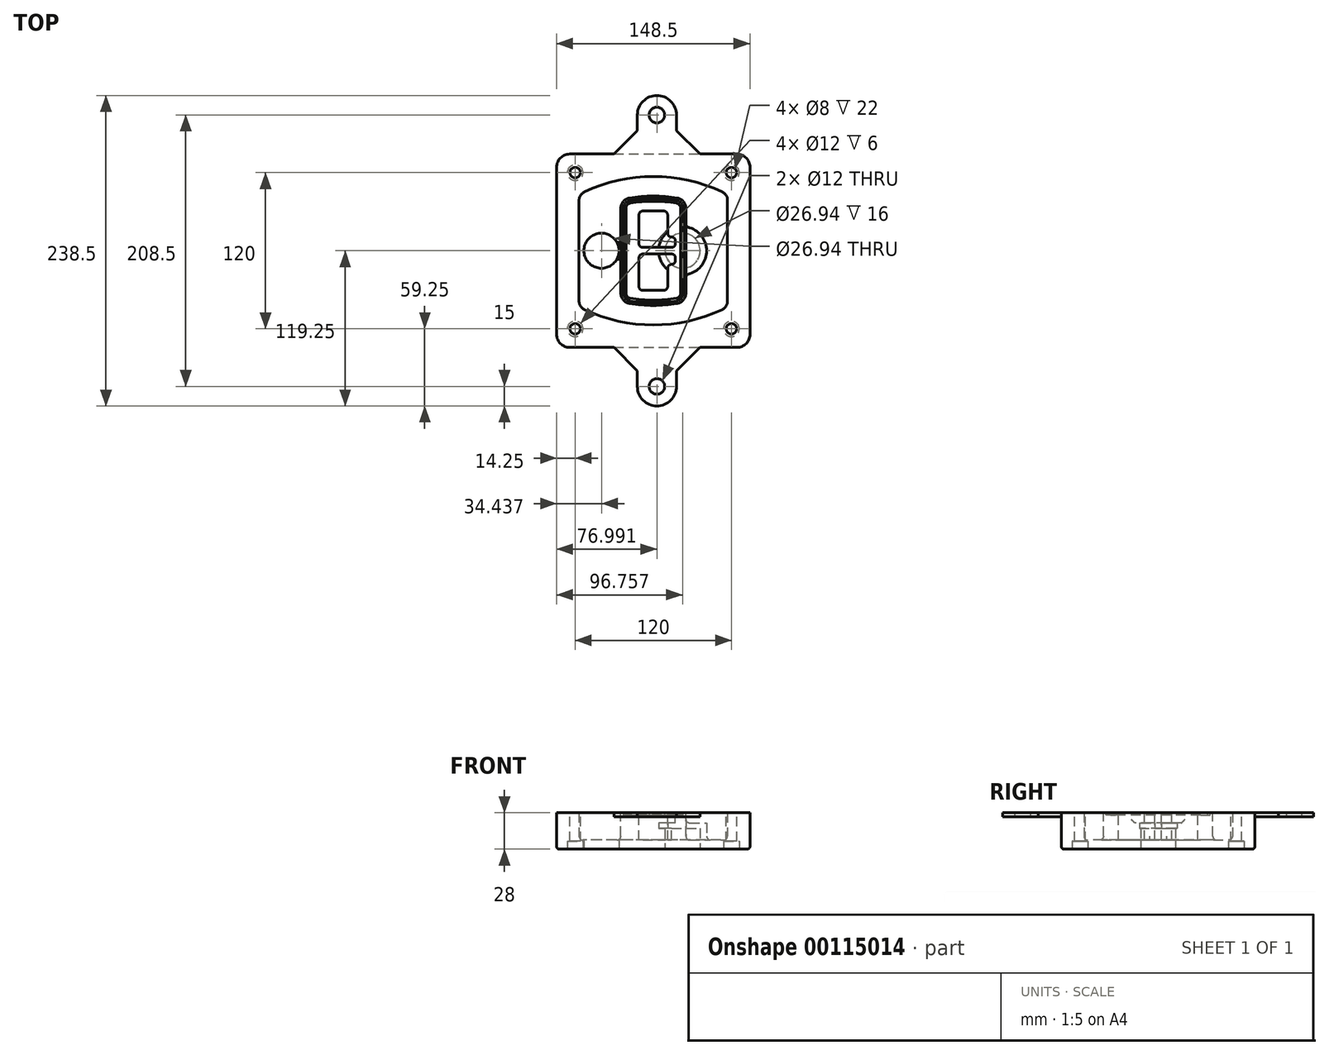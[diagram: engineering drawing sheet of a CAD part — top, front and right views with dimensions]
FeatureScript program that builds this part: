
annotation { "Feature Type Name" : "Feature", "Feature Type Description" : "" }
export const myFeature = defineFeature(function(context is Context, id is Id, definition is map)
    precondition{}
    {
        {
            var Q0;
            Q0=qCreatedBy(makeId("Top.planeOp"),FACE);
            var sketch = newSketch(context, id + "F0", { "sketchPlane" : qUnion([Q0])});
            skPoint(sketch, "E0.rect.middle", {"position": v(0, 0) * mm});
            skLineSegment(sketch, "E1.bottom", {"start": v(-64.25, -74.25) * mm, "end": v(64.25, -74.25) * mm});
            skLineSegment(sketch, "E1.top", {"start": v(-64.25, 74.25) * mm, "end": v(64.25, 74.25) * mm});
            skLineSegment(sketch, "E1.left", {"start": v(-74.25, -64.25) * mm, "end": v(-74.25, 64.25) * mm});
            skLineSegment(sketch, "E1.right", {"start": v(74.25, -64.25) * mm, "end": v(74.25, 64.25) * mm});
            skLineSegment(sketch, "E2", {"start": v(-74.25, 74.25) * mm, "end": v(74.25, -74.25) * mm, "construction": true});
            skLineSegment(sketch, "E3", {"start": v(74.25, 74.25) * mm, "end": v(-74.25, -74.25) * mm, "construction": true});
            skCircle(sketch, "E4", {"center": v(-60, 60) * mm, "radius": 4 * mm});
            skCircle(sketch, "E5", {"center": v(60, 60) * mm, "radius": 4 * mm});
            skCircle(sketch, "E6", {"center": v(60, -60) * mm, "radius": 4 * mm});
            skCircle(sketch, "E7", {"center": v(-60, -60) * mm, "radius": 4 * mm});
            skLineSegment(sketch, "E8", {"start": v(-60, 60) * mm, "end": v(60, 60) * mm, "construction": true});
            skLineSegment(sketch, "E9", {"start": v(60, 60) * mm, "end": v(60, -60) * mm, "construction": true});
            skLineSegment(sketch, "E10", {"start": v(60, -60) * mm, "end": v(-60, -60) * mm, "construction": true});
            skLineSegment(sketch, "E11", {"start": v(-60, -60) * mm, "end": v(-60, 60) * mm, "construction": true});
            skLineSegment(sketch, "E12", {"start": v(-60, 38.83) * mm, "end": v(-60, -38.83) * mm});
            skLineSegment(sketch, "E13", {"start": v(60, 38.83) * mm, "end": v(60, -38.83) * mm});
            skArc(sketch, "E14", {"start": v(54.26, 47.88) * mm, "mid": v(0, 60) * mm, "end": v(-54.26, 47.88) * mm});
            skArc(sketch, "E15", {"start": v(-54.26, -47.88) * mm, "mid": v(0, -60) * mm, "end": v(54.26, -47.88) * mm});
            skLineSegment(sketch, "E16", {"start": v(-60, 0) * mm, "end": v(60, 0) * mm, "construction": true});
            skPoint(sketch, "E17.visualSharp", {"position": v(-60, -45) * mm});
            skArc(sketch, "E17.filletArc", {"start": v(-60, -38.83) * mm, "mid": v(-58.44, -44.2) * mm, "end": v(-54.26, -47.88) * mm});
            skPoint(sketch, "E18.visualSharp", {"position": v(-60, 45) * mm});
            skArc(sketch, "E18.filletArc", {"start": v(-54.26, 47.88) * mm, "mid": v(-58.44, 44.2) * mm, "end": v(-60, 38.83) * mm});
            skPoint(sketch, "E19.visualSharp", {"position": v(60, 45) * mm});
            skArc(sketch, "E19.filletArc", {"start": v(60, 38.83) * mm, "mid": v(58.44, 44.2) * mm, "end": v(54.26, 47.88) * mm});
            skPoint(sketch, "E20.visualSharp", {"position": v(60, -45) * mm});
            skArc(sketch, "E20.filletArc", {"start": v(54.26, -47.88) * mm, "mid": v(58.44, -44.2) * mm, "end": v(60, -38.83) * mm});
            skPoint(sketch, "E21.visualSharp", {"position": v(-74.25, 74.25) * mm});
            skArc(sketch, "E21.filletArc", {"start": v(-64.25, 74.25) * mm, "mid": v(-71.32, 71.32) * mm, "end": v(-74.25, 64.25) * mm});
            skPoint(sketch, "E22.visualSharp", {"position": v(74.25, 74.25) * mm});
            skArc(sketch, "E22.filletArc", {"start": v(74.25, 64.25) * mm, "mid": v(71.32, 71.32) * mm, "end": v(64.25, 74.25) * mm});
            skPoint(sketch, "E23.visualSharp", {"position": v(74.25, -74.25) * mm});
            skArc(sketch, "E23.filletArc", {"start": v(64.25, -74.25) * mm, "mid": v(71.32, -71.32) * mm, "end": v(74.25, -64.25) * mm});
            skPoint(sketch, "E24.visualSharp", {"position": v(-74.25, -74.25) * mm});
            skArc(sketch, "E24.filletArc", {"start": v(-74.25, -64.25) * mm, "mid": v(-71.32, -71.32) * mm, "end": v(-64.25, -74.25) * mm});
            skArc(sketch, "E25.0", {"start": v(57, 38.83) * mm, "mid": v(55.9, 42.58) * mm, "end": v(52.98, 45.17) * mm});
            skLineSegment(sketch, "E25.1", {"start": v(57, 38.83) * mm, "end": v(57, -38.83) * mm});
            skArc(sketch, "E25.2", {"start": v(52.98, -45.17) * mm, "mid": v(55.9, -42.58) * mm, "end": v(57, -38.83) * mm});
            skArc(sketch, "E25.3", {"start": v(-52.98, -45.17) * mm, "mid": v(0, -57) * mm, "end": v(52.98, -45.17) * mm});
            skArc(sketch, "E25.4", {"start": v(-57, -38.83) * mm, "mid": v(-55.9, -42.58) * mm, "end": v(-52.98, -45.17) * mm});
            skArc(sketch, "E25.5", {"start": v(52.98, 45.17) * mm, "mid": v(0, 57) * mm, "end": v(-52.98, 45.17) * mm});
            skLineSegment(sketch, "E25.6", {"start": v(-57, 38.83) * mm, "end": v(-57, -38.83) * mm});
            skArc(sketch, "E25.7", {"start": v(-52.98, 45.17) * mm, "mid": v(-55.9, 42.58) * mm, "end": v(-57, 38.83) * mm});
            skArc(sketch, "E26.0", {"start": v(-55.96, 51.5) * mm, "mid": v(-61.82, 46.33) * mm, "end": v(-64, 38.83) * mm});
            skArc(sketch, "E26.1", {"start": v(55.96, 51.5) * mm, "mid": v(0, 64) * mm, "end": v(-55.96, 51.5) * mm});
            skArc(sketch, "E26.2", {"start": v(64, 38.83) * mm, "mid": v(61.82, 46.33) * mm, "end": v(55.96, 51.5) * mm});
            skLineSegment(sketch, "E26.3", {"start": v(64, 38.83) * mm, "end": v(64, -38.83) * mm});
            skArc(sketch, "E26.4", {"start": v(55.96, -51.5) * mm, "mid": v(61.82, -46.33) * mm, "end": v(64, -38.83) * mm});
            skLineSegment(sketch, "E26.5", {"start": v(-64, 38.83) * mm, "end": v(-64, -38.83) * mm});
            skArc(sketch, "E26.6", {"start": v(-55.96, -51.5) * mm, "mid": v(0, -64) * mm, "end": v(55.96, -51.5) * mm});
            skArc(sketch, "E26.7", {"start": v(-64, -38.83) * mm, "mid": v(-61.82, -46.33) * mm, "end": v(-55.96, -51.5) * mm});
            skSolve(sketch);
        }
        {
            var Q0;
            Q0=makeQuery(id+"F0.imprint","IMPRINT",FACE,{"disambiguationData":[TD([[makeQuery(id+"F0.imprint","IMPRINT",EDGE,{"derivedFrom":sQuery(id+"F0.wireOp",EDGE,"E1.bottom")}),1.0]])]});
            var Q1;
            Q1=makeQuery(id+"F0.imprint","IMPRINT",FACE,{"disambiguationData":[TD([[makeQuery(id+"F0.imprint","IMPRINT",EDGE,{"derivedFrom":sQuery(id+"F0.wireOp",EDGE,"E12")}),1.0]])]});
            var Q2;
            Q2=makeQuery(id+"F0.imprint","IMPRINT",FACE,{"disambiguationData":[TD([[makeQuery(id+"F0.imprint","IMPRINT",EDGE,{"derivedFrom":sQuery(id+"F0.wireOp",EDGE,"E25.0")}),1.0]])]});
            var Q3;
            Q3=makeQuery(id+"F0.imprint","IMPRINT",FACE,{"disambiguationData":[TD([[makeQuery(id+"F0.imprint","IMPRINT",EDGE,{"derivedFrom":sQuery(id+"F0.wireOp",EDGE,"E12")}),-1.0]])]});
            extrude(context, id + "F1", {"entities" : qUnion([Q0, Q1, Q2, Q3]), "oppositeDirection" : true, "depth" : 25 * mm});
        }
        {
            var Q0;
            Q0=makeQuery(id+"F0.imprint","IMPRINT",FACE,{"disambiguationData":[TD([[makeQuery(id+"F0.imprint","IMPRINT",EDGE,{"derivedFrom":sQuery(id+"F0.wireOp",EDGE,"E12")}),1.0]])]});
            extrude(context, id + "F2", {"entities" : qUnion([Q0]), "operationType" : NewBodyOperationType.ADD, "depth" : 3 * mm});
        }
        {
            var Q0;
            Q0=makeQuery(id+"F0.imprint","IMPRINT",FACE,{"disambiguationData":[TD([[makeQuery(id+"F0.imprint","IMPRINT",EDGE,{"derivedFrom":sQuery(id+"F0.wireOp",EDGE,"E25.0")}),1.0]])]});
            extrude(context, id + "F3", {"entities" : qUnion([Q0]), "operationType" : NewBodyOperationType.REMOVE, "oppositeDirection" : true, "depth" : 18 * mm});
        }
        {
            var Q0;
            Q0=makeQuery(id+"F2.opExtrude","CAP_FACE",FACE,{"disambiguationData":[OSD([sQuery(id+"F0.wireOp",EDGE,"E12"),sQuery(id+"F0.wireOp",EDGE,"E13"),sQuery(id+"F0.wireOp",EDGE,"E14"),sQuery(id+"F0.wireOp",EDGE,"E15"),sQuery(id+"F0.wireOp",EDGE,"E17.filletArc"),sQuery(id+"F0.wireOp",EDGE,"E18.filletArc"),sQuery(id+"F0.wireOp",EDGE,"E19.filletArc"),sQuery(id+"F0.wireOp",EDGE,"E20.filletArc"),sQuery(id+"F0.wireOp",EDGE,"E25.0"),sQuery(id+"F0.wireOp",EDGE,"E25.1"),sQuery(id+"F0.wireOp",EDGE,"E25.2"),sQuery(id+"F0.wireOp",EDGE,"E25.3"),sQuery(id+"F0.wireOp",EDGE,"E25.4"),sQuery(id+"F0.wireOp",EDGE,"E25.5"),sQuery(id+"F0.wireOp",EDGE,"E25.6"),sQuery(id+"F0.wireOp",EDGE,"E25.7")])],"isStart":false});
            var sketch = newSketch(context, id + "F4", { "sketchPlane" : qUnion([Q0])});
            skArc(sketch, "E27.0", {"start": v(-18.34, -40.45) * mm, "mid": v(0, -42) * mm, "end": v(18.34, -40.45) * mm});
            skArc(sketch, "E28.0", {"start": v(18.34, 40.45) * mm, "mid": v(0, 42) * mm, "end": v(-18.34, 40.45) * mm});
            skLineSegment(sketch, "E29", {"start": v(-25, 32.57) * mm, "end": v(-25, -32.57) * mm});
            skLineSegment(sketch, "E30", {"start": v(25, 32.57) * mm, "end": v(25, -32.57) * mm});
            skLineSegment(sketch, "E31", {"start": v(-25, 39.1) * mm, "end": v(25, 39.1) * mm, "construction": true});
            skLineSegment(sketch, "E32", {"start": v(-25, -39.1) * mm, "end": v(25, -39.1) * mm, "construction": true});
            skPoint(sketch, "E33.visualSharp", {"position": v(-25, 39.1) * mm});
            skArc(sketch, "E33.filletArc", {"start": v(-18.34, 40.45) * mm, "mid": v(-23.11, 37.73) * mm, "end": v(-25, 32.57) * mm});
            skPoint(sketch, "E34.visualSharp", {"position": v(25, 39.1) * mm});
            skArc(sketch, "E34.filletArc", {"start": v(25, 32.57) * mm, "mid": v(23.11, 37.73) * mm, "end": v(18.34, 40.45) * mm});
            skPoint(sketch, "E35.visualSharp", {"position": v(25, -39.1) * mm});
            skArc(sketch, "E35.filletArc", {"start": v(18.34, -40.45) * mm, "mid": v(23.11, -37.73) * mm, "end": v(25, -32.57) * mm});
            skPoint(sketch, "E36.visualSharp", {"position": v(-25, -39.1) * mm});
            skArc(sketch, "E36.filletArc", {"start": v(-25, -32.57) * mm, "mid": v(-23.11, -37.73) * mm, "end": v(-18.34, -40.45) * mm});
            skArc(sketch, "E37.0", {"start": v(52.98, 45.17) * mm, "mid": v(0, 57) * mm, "end": v(-52.98, 45.17) * mm});
            skArc(sketch, "E37.1", {"start": v(-52.98, 45.17) * mm, "mid": v(-55.9, 42.58) * mm, "end": v(-57, 38.83) * mm});
            skLineSegment(sketch, "E37.2", {"start": v(-57, 38.83) * mm, "end": v(-57, -38.83) * mm});
            skArc(sketch, "E37.3", {"start": v(-57, -38.83) * mm, "mid": v(-55.9, -42.58) * mm, "end": v(-52.98, -45.17) * mm});
            skArc(sketch, "E37.4", {"start": v(-52.98, -45.17) * mm, "mid": v(0, -57) * mm, "end": v(52.98, -45.17) * mm});
            skArc(sketch, "E37.5", {"start": v(52.98, -45.17) * mm, "mid": v(55.9, -42.58) * mm, "end": v(57, -38.83) * mm});
            skLineSegment(sketch, "E37.6", {"start": v(57, 38.83) * mm, "end": v(57, -38.83) * mm});
            skArc(sketch, "E37.7", {"start": v(57, 38.83) * mm, "mid": v(55.9, 42.58) * mm, "end": v(52.98, 45.17) * mm});
            skLineSegment(sketch, "E38.0", {"start": v(23, 32.57) * mm, "end": v(23, -32.57) * mm});
            skArc(sketch, "E38.1", {"start": v(18, -38.48) * mm, "mid": v(21.58, -36.44) * mm, "end": v(23, -32.57) * mm});
            skArc(sketch, "E38.2", {"start": v(-18, -38.48) * mm, "mid": v(0, -40) * mm, "end": v(18, -38.48) * mm});
            skArc(sketch, "E38.3", {"start": v(-23, -32.57) * mm, "mid": v(-21.58, -36.44) * mm, "end": v(-18, -38.48) * mm});
            skLineSegment(sketch, "E38.4", {"start": v(-23, 32.57) * mm, "end": v(-23, -32.57) * mm});
            skArc(sketch, "E38.5", {"start": v(23, 32.57) * mm, "mid": v(21.58, 36.44) * mm, "end": v(18, 38.48) * mm});
            skArc(sketch, "E38.6", {"start": v(-18, 38.48) * mm, "mid": v(-21.58, 36.44) * mm, "end": v(-23, 32.57) * mm});
            skArc(sketch, "E38.7", {"start": v(18, 38.48) * mm, "mid": v(0, 40) * mm, "end": v(-18, 38.48) * mm});
            skArc(sketch, "E39.0", {"start": v(21, 32.57) * mm, "mid": v(20.06, 35.15) * mm, "end": v(17.67, 36.5) * mm});
            skLineSegment(sketch, "E39.1", {"start": v(21, 32.57) * mm, "end": v(21, -32.57) * mm});
            skArc(sketch, "E39.2", {"start": v(17.67, -36.5) * mm, "mid": v(20.06, -35.15) * mm, "end": v(21, -32.57) * mm});
            skArc(sketch, "E39.3", {"start": v(-17.67, -36.5) * mm, "mid": v(0, -38) * mm, "end": v(17.67, -36.5) * mm});
            skArc(sketch, "E39.4", {"start": v(-21, -32.57) * mm, "mid": v(-20.06, -35.15) * mm, "end": v(-17.67, -36.5) * mm});
            skArc(sketch, "E39.5", {"start": v(17.67, 36.5) * mm, "mid": v(0, 38) * mm, "end": v(-17.67, 36.5) * mm});
            skLineSegment(sketch, "E39.6", {"start": v(-21, 32.57) * mm, "end": v(-21, -32.57) * mm});
            skArc(sketch, "E39.7", {"start": v(-17.67, 36.5) * mm, "mid": v(-20.06, 35.15) * mm, "end": v(-21, 32.57) * mm});
            skLineSegment(sketch, "E40", {"start": v(-25, 0) * mm, "end": v(25, 0) * mm, "construction": true});
            skLineSegment(sketch, "E41", {"start": v(-11, 5.5) * mm, "end": v(-11, 27.5) * mm});
            skLineSegment(sketch, "E42", {"start": v(-8, 30.5) * mm, "end": v(8, 30.5) * mm});
            skLineSegment(sketch, "E43", {"start": v(11, 27.5) * mm, "end": v(11, 13.5) * mm});
            skLineSegment(sketch, "E44", {"start": v(14, 10.5) * mm, "end": v(14, 10.5) * mm});
            skLineSegment(sketch, "E45", {"start": v(17, 7.5) * mm, "end": v(17, 5.5) * mm});
            skLineSegment(sketch, "E46", {"start": v(14, 2.5) * mm, "end": v(-8, 2.5) * mm});
            skPoint(sketch, "E47.visualSharp", {"position": v(-11, 30.5) * mm});
            skArc(sketch, "E47.filletArc", {"start": v(-8, 30.5) * mm, "mid": v(-10.12, 29.62) * mm, "end": v(-11, 27.5) * mm});
            skPoint(sketch, "E48.visualSharp", {"position": v(11, 30.5) * mm});
            skArc(sketch, "E48.filletArc", {"start": v(11, 27.5) * mm, "mid": v(10.12, 29.62) * mm, "end": v(8, 30.5) * mm});
            skPoint(sketch, "E49.visualSharp", {"position": v(11, 10.5) * mm});
            skArc(sketch, "E49.filletArc", {"start": v(11, 13.5) * mm, "mid": v(11.88, 11.38) * mm, "end": v(14, 10.5) * mm});
            skPoint(sketch, "E50.visualSharp", {"position": v(17, 10.5) * mm});
            skArc(sketch, "E50.filletArc", {"start": v(17, 7.5) * mm, "mid": v(16.12, 9.62) * mm, "end": v(14, 10.5) * mm});
            skPoint(sketch, "E51.visualSharp", {"position": v(17, 2.5) * mm});
            skArc(sketch, "E51.filletArc", {"start": v(14, 2.5) * mm, "mid": v(16.12, 3.38) * mm, "end": v(17, 5.5) * mm});
            skPoint(sketch, "E52.visualSharp", {"position": v(-11, 2.5) * mm});
            skArc(sketch, "E52.filletArc", {"start": v(-11, 5.5) * mm, "mid": v(-10.12, 3.38) * mm, "end": v(-8, 2.5) * mm});
            skLineSegment(sketch, "E53.0.MirrorCS", {"start": v(14, -2.5) * mm, "end": v(-8, -2.5) * mm});
            skArc(sketch, "E54.0.MirrorCS", {"start": v(-11, -5.5) * mm, "mid": v(-10.12, -3.38) * mm, "end": v(-8, -2.5) * mm});
            skLineSegment(sketch, "E55.0.MirrorCS", {"start": v(-11, -5.5) * mm, "end": v(-11, -27.5) * mm});
            skArc(sketch, "E56.0.MirrorCS", {"start": v(-8, -30.5) * mm, "mid": v(-10.12, -29.62) * mm, "end": v(-11, -27.5) * mm});
            skLineSegment(sketch, "E57.0.MirrorCS", {"start": v(-8, -30.5) * mm, "end": v(8, -30.5) * mm});
            skArc(sketch, "E58.0.MirrorCS", {"start": v(11, -27.5) * mm, "mid": v(10.12, -29.62) * mm, "end": v(8, -30.5) * mm});
            skLineSegment(sketch, "E59.0.MirrorCS", {"start": v(11, -27.5) * mm, "end": v(11, -13.5) * mm});
            skArc(sketch, "E60.0.MirrorCS", {"start": v(11, -13.5) * mm, "mid": v(11.88, -11.38) * mm, "end": v(14, -10.5) * mm});
            skArc(sketch, "E61.0.MirrorCS", {"start": v(17, -7.5) * mm, "mid": v(16.12, -9.62) * mm, "end": v(14, -10.5) * mm});
            skLineSegment(sketch, "E62.0.MirrorCS", {"start": v(17, -7.5) * mm, "end": v(17, -5.5) * mm});
            skArc(sketch, "E63.0.MirrorCS", {"start": v(14, -2.5) * mm, "mid": v(16.12, -3.38) * mm, "end": v(17, -5.5) * mm});
            skSolve(sketch);
        }
        {
            var Q0;
            Q0=makeQuery(id+"F4.imprint","IMPRINT",FACE,{"disambiguationData":[TD([[makeQuery(id+"F4.imprint","IMPRINT",EDGE,{"derivedFrom":sQuery(id+"F4.wireOp",EDGE,"E27.0")}),1.0]])]});
            var Q1;
            Q1=makeQuery(id+"F4.imprint","IMPRINT",FACE,{"disambiguationData":[TD([[makeQuery(id+"F4.imprint","IMPRINT",EDGE,{"derivedFrom":sQuery(id+"F4.wireOp",EDGE,"E38.0")}),-1.0]])]});
            var Q2;
            Q2=makeQuery(id+"F4.imprint","IMPRINT",FACE,{"disambiguationData":[TD([[makeQuery(id+"F4.imprint","IMPRINT",EDGE,{"derivedFrom":sQuery(id+"F4.wireOp",EDGE,"E39.0")}),1.0]])]});
            extrude(context, id + "F5", {"entities" : qUnion([Q0, Q1, Q2]), "operationType" : NewBodyOperationType.ADD, "endBound" : BoundingType.UP_TO_NEXT, "oppositeDirection" : true, "depth" : 25 * mm});
        }
        {
            var Q0;
            Q0=makeQuery(id+"F4.imprint","IMPRINT",FACE,{"disambiguationData":[TD([[makeQuery(id+"F4.imprint","IMPRINT",EDGE,{"derivedFrom":sQuery(id+"F4.wireOp",EDGE,"E38.0")}),-1.0]])]});
            extrude(context, id + "F6", {"entities" : qUnion([Q0]), "operationType" : NewBodyOperationType.REMOVE, "oppositeDirection" : true, "depth" : 2 * mm});
        }
        {
            var Q0;
            Q0=makeQuery(id+"F1.opExtrude","CAP_FACE",FACE,{"disambiguationData":[OSD([sQuery(id+"F0.wireOp",EDGE,"E1.bottom"),sQuery(id+"F0.wireOp",EDGE,"E1.top"),sQuery(id+"F0.wireOp",EDGE,"E1.left"),sQuery(id+"F0.wireOp",EDGE,"E1.right"),sQuery(id+"F0.wireOp",EDGE,"E4"),sQuery(id+"F0.wireOp",EDGE,"E5"),sQuery(id+"F0.wireOp",EDGE,"E6"),sQuery(id+"F0.wireOp",EDGE,"E7"),sQuery(id+"F0.wireOp",EDGE,"E21.filletArc"),sQuery(id+"F0.wireOp",EDGE,"E22.filletArc"),sQuery(id+"F0.wireOp",EDGE,"E23.filletArc"),sQuery(id+"F0.wireOp",EDGE,"E24.filletArc")])],"isStart":false});
            var sketch = newSketch(context, id + "F7", { "sketchPlane" : qUnion([Q0])});
            skCircle(sketch, "E64", {"center": v(22.5, 0) * mm, "radius": 13.47 * mm});
            skCircle(sketch, "E65", {"center": v(-39.81, 0) * mm, "radius": 13.47 * mm});
            skLineSegment(sketch, "E66", {"start": v(74.25, 0) * mm, "end": v(-74.25, 0) * mm});
            skCircle(sketch, "E67", {"center": v(22.5, 0) * mm, "radius": 18.47 * mm});
            skCircle(sketch, "E68", {"center": v(60, -60) * mm, "radius": 6 * mm});
            skCircle(sketch, "E69", {"center": v(-60, -60) * mm, "radius": 6 * mm});
            skCircle(sketch, "E70", {"center": v(-60, 60) * mm, "radius": 6 * mm});
            skCircle(sketch, "E71", {"center": v(60, 60) * mm, "radius": 6 * mm});
            skSolve(sketch);
        }
        {
            var Q0;
            {var subQ1=sQuery(id+"F7.wireOp",EDGE,"E66");var subQ4=sQuery(id+"F7.wireOp",EDGE,"E64");var subQ6=makeQuery(id+"F7.imprint","INTERSECT",VERTEX,{"disambiguationData":[OD(0.0)],"derivedFrom":[subQ4,subQ1]});Q0=makeQuery(id+"F7.imprint","IMPRINT",FACE,{"disambiguationData":[TD([[makeQuery(id+"F7.imprint","IMPRINT",EDGE,{"disambiguationData":[TD([[subQ6,-1.0]])],"derivedFrom":subQ4}),-1.0]])]});}
            var Q1;
            {var subQ0=sQuery(id+"F7.wireOp",EDGE,"E66");var subQ1=sQuery(id+"F7.wireOp",EDGE,"E64");var subQ3=makeQuery(id+"F7.imprint","INTERSECT",VERTEX,{"disambiguationData":[OD(0.0)],"derivedFrom":[subQ1,subQ0]});Q1=makeQuery(id+"F7.imprint","IMPRINT",FACE,{"disambiguationData":[TD([[makeQuery(id+"F7.imprint","IMPRINT",EDGE,{"disambiguationData":[TD([[subQ3,-1.0]])],"derivedFrom":subQ1}),1.0]])]});}
            var Q2;
            {var subQ0=sQuery(id+"F7.wireOp",EDGE,"E66");var subQ1=sQuery(id+"F7.wireOp",EDGE,"E64");var subQ3=makeQuery(id+"F7.imprint","INTERSECT",VERTEX,{"disambiguationData":[OD(0.0)],"derivedFrom":[subQ1,subQ0]});Q2=makeQuery(id+"F7.imprint","IMPRINT",FACE,{"disambiguationData":[TD([[makeQuery(id+"F7.imprint","IMPRINT",EDGE,{"disambiguationData":[TD([[subQ3,1.0]])],"derivedFrom":subQ1}),1.0]])]});}
            var Q3;
            {var subQ1=sQuery(id+"F7.wireOp",EDGE,"E66");var subQ4=sQuery(id+"F7.wireOp",EDGE,"E64");var subQ6=makeQuery(id+"F7.imprint","INTERSECT",VERTEX,{"disambiguationData":[OD(0.0)],"derivedFrom":[subQ4,subQ1]});Q3=makeQuery(id+"F7.imprint","IMPRINT",FACE,{"disambiguationData":[TD([[makeQuery(id+"F7.imprint","IMPRINT",EDGE,{"disambiguationData":[TD([[subQ6,1.0]])],"derivedFrom":subQ4}),-1.0]])]});}
            extrude(context, id + "F8", {"entities" : qUnion([Q0, Q1, Q2, Q3]), "operationType" : NewBodyOperationType.ADD, "oppositeDirection" : true, "depth" : 20 * mm});
        }
        {
            var Q0;
            {var subQ0=sQuery(id+"F7.wireOp",EDGE,"E66");var subQ1=sQuery(id+"F7.wireOp",EDGE,"E64");var subQ3=makeQuery(id+"F7.imprint","INTERSECT",VERTEX,{"disambiguationData":[OD(0.0)],"derivedFrom":[subQ1,subQ0]});Q0=makeQuery(id+"F7.imprint","IMPRINT",FACE,{"disambiguationData":[TD([[makeQuery(id+"F7.imprint","IMPRINT",EDGE,{"disambiguationData":[TD([[subQ3,-1.0]])],"derivedFrom":subQ1}),1.0]])]});}
            var Q1;
            {var subQ0=sQuery(id+"F7.wireOp",EDGE,"E66");var subQ1=sQuery(id+"F7.wireOp",EDGE,"E64");var subQ3=makeQuery(id+"F7.imprint","INTERSECT",VERTEX,{"disambiguationData":[OD(0.0)],"derivedFrom":[subQ1,subQ0]});Q1=makeQuery(id+"F7.imprint","IMPRINT",FACE,{"disambiguationData":[TD([[makeQuery(id+"F7.imprint","IMPRINT",EDGE,{"disambiguationData":[TD([[subQ3,1.0]])],"derivedFrom":subQ1}),1.0]])]});}
            extrude(context, id + "F9", {"entities" : qUnion([Q0, Q1]), "operationType" : NewBodyOperationType.REMOVE, "oppositeDirection" : true, "depth" : 16 * mm});
        }
        {
            var Q0;
            {var subQ0=sQuery(id+"F7.wireOp",EDGE,"E66");var subQ1=sQuery(id+"F7.wireOp",EDGE,"E65");var subQ3=makeQuery(id+"F7.imprint","INTERSECT",VERTEX,{"disambiguationData":[OD(0.0)],"derivedFrom":[subQ1,subQ0]});Q0=makeQuery(id+"F7.imprint","IMPRINT",FACE,{"disambiguationData":[TD([[makeQuery(id+"F7.imprint","IMPRINT",EDGE,{"disambiguationData":[TD([[subQ3,-1.0]])],"derivedFrom":subQ1}),1.0]])]});}
            var Q1;
            {var subQ0=sQuery(id+"F7.wireOp",EDGE,"E66");var subQ1=sQuery(id+"F7.wireOp",EDGE,"E65");var subQ3=makeQuery(id+"F7.imprint","INTERSECT",VERTEX,{"disambiguationData":[OD(0.0)],"derivedFrom":[subQ1,subQ0]});Q1=makeQuery(id+"F7.imprint","IMPRINT",FACE,{"disambiguationData":[TD([[makeQuery(id+"F7.imprint","IMPRINT",EDGE,{"disambiguationData":[TD([[subQ3,1.0]])],"derivedFrom":subQ1}),1.0]])]});}
            extrude(context, id + "F10", {"entities" : qUnion([Q0, Q1]), "operationType" : NewBodyOperationType.REMOVE, "oppositeDirection" : true, "depth" : 25 * mm});
        }
        {
            var Q0;
            Q0=makeQuery(id+"F7.imprint","IMPRINT",FACE,{"disambiguationData":[TD([[makeQuery(id+"F7.imprint","IMPRINT",EDGE,{"derivedFrom":sQuery(id+"F7.wireOp",EDGE,"E68")}),1.0]])]});
            var Q1;
            Q1=makeQuery(id+"F7.imprint","IMPRINT",FACE,{"disambiguationData":[TD([[makeQuery(id+"F7.imprint","IMPRINT",EDGE,{"derivedFrom":makeQuery(id+"F1.opExtrude","CAP_EDGE",EDGE,{"disambiguationData":[OSD([sQuery(id+"F0.wireOp",EDGE,"E5")])],"isStart":false})}),-1.0]])]});
            var Q2;
            Q2=makeQuery(id+"F7.imprint","IMPRINT",FACE,{"disambiguationData":[TD([[makeQuery(id+"F7.imprint","IMPRINT",EDGE,{"derivedFrom":sQuery(id+"F7.wireOp",EDGE,"E69")}),1.0]])]});
            var Q3;
            Q3=makeQuery(id+"F7.imprint","IMPRINT",FACE,{"disambiguationData":[TD([[makeQuery(id+"F7.imprint","IMPRINT",EDGE,{"derivedFrom":makeQuery(id+"F1.opExtrude","CAP_EDGE",EDGE,{"disambiguationData":[OSD([sQuery(id+"F0.wireOp",EDGE,"E4")])],"isStart":false})}),-1.0]])]});
            var Q4;
            Q4=makeQuery(id+"F7.imprint","IMPRINT",FACE,{"disambiguationData":[TD([[makeQuery(id+"F7.imprint","IMPRINT",EDGE,{"derivedFrom":sQuery(id+"F7.wireOp",EDGE,"E70")}),1.0]])]});
            var Q5;
            Q5=makeQuery(id+"F7.imprint","IMPRINT",FACE,{"disambiguationData":[TD([[makeQuery(id+"F7.imprint","IMPRINT",EDGE,{"derivedFrom":makeQuery(id+"F1.opExtrude","CAP_EDGE",EDGE,{"disambiguationData":[OSD([sQuery(id+"F0.wireOp",EDGE,"E7")])],"isStart":false})}),-1.0]])]});
            var Q6;
            Q6=makeQuery(id+"F7.imprint","IMPRINT",FACE,{"disambiguationData":[TD([[makeQuery(id+"F7.imprint","IMPRINT",EDGE,{"derivedFrom":sQuery(id+"F7.wireOp",EDGE,"E71")}),1.0]])]});
            var Q7;
            Q7=makeQuery(id+"F7.imprint","IMPRINT",FACE,{"disambiguationData":[TD([[makeQuery(id+"F7.imprint","IMPRINT",EDGE,{"derivedFrom":makeQuery(id+"F1.opExtrude","CAP_EDGE",EDGE,{"disambiguationData":[OSD([sQuery(id+"F0.wireOp",EDGE,"E6")])],"isStart":false})}),-1.0]])]});
            extrude(context, id + "F11", {"entities" : qUnion([Q0, Q1, Q2, Q3, Q4, Q5, Q6, Q7]), "operationType" : NewBodyOperationType.REMOVE, "oppositeDirection" : true, "depth" : 6 * mm});
        }
        {
            var Q0;
            Q0=makeQuery(id+"F9.boolean.opBoolean","COPY",FACE,{"derivedFrom":makeQuery(id+"F9.opExtrude","CAP_FACE",FACE,{"disambiguationData":[OSD([sQuery(id+"F7.wireOp",EDGE,"E64")])],"isStart":false})});
            var sketch = newSketch(context, id + "F12", { "sketchPlane" : qUnion([Q0])});
            skArc(sketch, "E72.0", {"start": v(11, 14.45) * mm, "mid": v(6.45, 9.13) * mm, "end": v(4.2, 2.5) * mm});
            skArc(sketch, "E72.1", {"start": v(4.2, -2.5) * mm, "mid": v(6.45, -9.13) * mm, "end": v(11, -14.45) * mm});
            skLineSegment(sketch, "E73", {"start": v(4.2, -2.5) * mm, "end": v(14, -2.5) * mm});
            skLineSegment(sketch, "E74.0", {"start": v(14, 2.5) * mm, "end": v(4.2, 2.5) * mm});
            skArc(sketch, "E74.1", {"start": v(14, 2.5) * mm, "mid": v(16.12, 3.38) * mm, "end": v(17, 5.5) * mm});
            skLineSegment(sketch, "E74.2", {"start": v(17, 7.5) * mm, "end": v(17, 5.5) * mm});
            skArc(sketch, "E74.3", {"start": v(17, 7.5) * mm, "mid": v(16.12, 9.62) * mm, "end": v(14, 10.5) * mm});
            skArc(sketch, "E74.4", {"start": v(11, 13.5) * mm, "mid": v(11.88, 11.38) * mm, "end": v(14, 10.5) * mm});
            skLineSegment(sketch, "E74.5", {"start": v(11, 14.45) * mm, "end": v(11, 13.5) * mm});
            skLineSegment(sketch, "E74.7", {"start": v(14, -2.5) * mm, "end": v(4.2, -2.5) * mm});
            skArc(sketch, "E74.8", {"start": v(14, -2.5) * mm, "mid": v(16.12, -3.38) * mm, "end": v(17, -5.5) * mm});
            skLineSegment(sketch, "E74.9", {"start": v(17, -7.5) * mm, "end": v(17, -5.5) * mm});
            skArc(sketch, "E74.10", {"start": v(17, -7.5) * mm, "mid": v(16.12, -9.62) * mm, "end": v(14, -10.5) * mm});
            skArc(sketch, "E74.11", {"start": v(11, -13.5) * mm, "mid": v(11.88, -11.38) * mm, "end": v(14, -10.5) * mm});
            skLineSegment(sketch, "E74.12", {"start": v(11, -14.45) * mm, "end": v(11, -13.5) * mm});
            skPoint(sketch, "E75.orphan", {"position": v(11, -27.5) * mm});
            skPoint(sketch, "E76.orphan", {"position": v(-8, -2.5) * mm});
            skPoint(sketch, "E77.orphan", {"position": v(-8, 2.5) * mm});
            skPoint(sketch, "E78.orphan", {"position": v(11, 27.5) * mm});
            skSolve(sketch);
        }
        {
            var Q0;
            {var subQ7=sQuery(id+"F12.wireOp",EDGE,"E72.0");var subQ14=sQuery(id+"F12.wireOp",EDGE,"E72.1");var subQ16=sQuery(id+"F12.wireOp",EDGE,"E74.1");var subQ18=sQuery(id+"F12.wireOp",EDGE,"E74.8");Q0=qUnion([makeQuery(id+"F12.imprint","IMPRINT",FACE,{"disambiguationData":[TD([[makeQuery(id+"F12.imprint","IMPRINT",EDGE,{"derivedFrom":subQ7}),1.0]])]}),makeQuery(id+"F12.imprint","IMPRINT",FACE,{"disambiguationData":[TD([[makeQuery(id+"F12.imprint","IMPRINT",EDGE,{"derivedFrom":subQ14}),1.0]])]}),makeQuery(id+"F12.imprint","IMPRINT",FACE,{"disambiguationData":[TD([[makeQuery(id+"F12.imprint","IMPRINT",EDGE,{"derivedFrom":subQ16}),1.0]])]}),makeQuery(id+"F12.imprint","IMPRINT",FACE,{"disambiguationData":[TD([[makeQuery(id+"F12.imprint","IMPRINT",EDGE,{"derivedFrom":subQ18}),-1.0]])]})]);}
            var Q1;
            Q1=makeQuery(id+"F5.boolean.opBoolean","SPLIT",FACE,{"disambiguationData":[TD([makeQuery(id+"F5.opExtrude","SWEPT_FACE",FACE,{"disambiguationData":[OSD([sQuery(id+"F4.wireOp",EDGE,"E41")])]})])],"derivedFrom":makeQuery(id+"F3.boolean.opBoolean","COPY",FACE,{"derivedFrom":makeQuery(id+"F3.opExtrude","CAP_FACE",FACE,{"disambiguationData":[OSD([sQuery(id+"F0.wireOp",EDGE,"E25.0"),sQuery(id+"F0.wireOp",EDGE,"E25.1"),sQuery(id+"F0.wireOp",EDGE,"E25.2"),sQuery(id+"F0.wireOp",EDGE,"E25.3"),sQuery(id+"F0.wireOp",EDGE,"E25.4"),sQuery(id+"F0.wireOp",EDGE,"E25.5"),sQuery(id+"F0.wireOp",EDGE,"E25.6"),sQuery(id+"F0.wireOp",EDGE,"E25.7")])],"isStart":false})})});
            extrude(context, id + "F13", {"entities" : qUnion([Q0]), "operationType" : NewBodyOperationType.REMOVE, "endBound" : BoundingType.UP_TO_SURFACE, "endBoundEntityFace" : qUnion([Q1]), "depth" : 25 * mm});
        }
        {
            var Q0;
            Q0=makeQuery(id+"F3.boolean.opBoolean","COPY",EDGE,{"derivedFrom":makeQuery(id+"F3.opExtrude","CAP_EDGE",EDGE,{"disambiguationData":[OSD([sQuery(id+"F0.wireOp",EDGE,"E25.6")])],"isStart":false})});
            var Q1;
            Q1=makeQuery(id+"F8.boolean.opBoolean","INTERSECT",EDGE,{"derivedFrom":[makeQuery(id+"F5.opExtrude","SWEPT_FACE",FACE,{"disambiguationData":[OSD([sQuery(id+"F4.wireOp",EDGE,"E30")])]}),makeQuery(id+"F8.opExtrude","CAP_FACE",FACE,{"disambiguationData":[OSD([sQuery(id+"F7.wireOp",EDGE,"E67")])],"isStart":false})]});
            var Q2;
            Q2=makeQuery(id+"F8.boolean.opBoolean","INTERSECT",EDGE,{"disambiguationData":[OD(1.0)],"derivedFrom":[makeQuery(id+"F5.opExtrude","SWEPT_FACE",FACE,{"disambiguationData":[OSD([sQuery(id+"F4.wireOp",EDGE,"E30")])]}),makeQuery(id+"F8.opExtrude","SWEPT_FACE",FACE,{"disambiguationData":[OSD([sQuery(id+"F7.wireOp",EDGE,"E67")])]})]});
            var Q3;
            {var subQ0=sQuery(id+"F4.wireOp",EDGE,"E30");Q3=makeQuery(id+"F8.boolean.opBoolean","SPLIT",EDGE,{"disambiguationData":[TD([makeQuery(id+"F5.opExtrude","SWEPT_FACE",FACE,{"disambiguationData":[OSD([sQuery(id+"F4.wireOp",EDGE,"E35.filletArc")])]})])],"derivedFrom":makeQuery(id+"F5.opExtrude","CAP_EDGE",EDGE,{"disambiguationData":[OSD([subQ0])],"isStart":false})});}
            var Q4;
            {var subQ0=sQuery(id+"F0.wireOp",EDGE,"E25.7");var subQ1=sQuery(id+"F0.wireOp",EDGE,"E25.1");var subQ2=sQuery(id+"F0.wireOp",EDGE,"E25.6");var subQ3=sQuery(id+"F0.wireOp",EDGE,"E25.5");var subQ4=sQuery(id+"F0.wireOp",EDGE,"E25.4");var subQ5=sQuery(id+"F0.wireOp",EDGE,"E25.0");var subQ6=sQuery(id+"F0.wireOp",EDGE,"E25.2");var subQ7=sQuery(id+"F0.wireOp",EDGE,"E25.3");Q4=makeQuery(id+"F8.boolean.opBoolean","INTERSECT",EDGE,{"derivedFrom":[makeQuery(id+"F5.boolean.opBoolean","SPLIT",FACE,{"disambiguationData":[TD([makeQuery(id+"F2.opExtrude","SWEPT_FACE",FACE,{"disambiguationData":[OSD([subQ5])]})])],"derivedFrom":makeQuery(id+"F3.boolean.opBoolean","COPY",FACE,{"derivedFrom":makeQuery(id+"F3.opExtrude","CAP_FACE",FACE,{"disambiguationData":[OSD([subQ5,subQ1,subQ6,subQ7,subQ4,subQ3,subQ2,subQ0])],"isStart":false})})}),makeQuery(id+"F8.opExtrude","SWEPT_FACE",FACE,{"disambiguationData":[OSD([sQuery(id+"F7.wireOp",EDGE,"E67")])]})]});}
            var Q5;
            Q5=makeQuery(id+"F8.boolean.opBoolean","INTERSECT",EDGE,{"disambiguationData":[OD(0.0)],"derivedFrom":[makeQuery(id+"F5.opExtrude","SWEPT_FACE",FACE,{"disambiguationData":[OSD([sQuery(id+"F4.wireOp",EDGE,"E30")])]}),makeQuery(id+"F8.opExtrude","SWEPT_FACE",FACE,{"disambiguationData":[OSD([sQuery(id+"F7.wireOp",EDGE,"E67")])]})]});
            fillet(context, id + "F14", {"entities" : qUnion([Q0, Q1, Q2, Q3, Q4, Q5]), "radius" : 3 * mm, "tangentPropagation" : true, "allowEdgeOverflow" : false});
        }
        {
            var Q0;
            Q0=makeQuery(id+"F1.opExtrude","CAP_EDGE",EDGE,{"disambiguationData":[OSD([sQuery(id+"F0.wireOp",EDGE,"E1.bottom")])],"isStart":false});
            fillet(context, id + "F15", {"entities" : qUnion([Q0]), "radius" : 2 * mm, "tangentPropagation" : true, "allowEdgeOverflow" : false});
        }
        {
            var Q0;
            {var subQ0=sQuery(id+"F0.wireOp",EDGE,"E22.filletArc");var subQ1=sQuery(id+"F0.wireOp",EDGE,"E7");var subQ2=sQuery(id+"F0.wireOp",EDGE,"E6");var subQ3=sQuery(id+"F0.wireOp",EDGE,"E5");var subQ4=sQuery(id+"F0.wireOp",EDGE,"E4");var subQ5=sQuery(id+"F0.wireOp",EDGE,"E1.bottom");var subQ6=sQuery(id+"F0.wireOp",EDGE,"E21.filletArc");var subQ7=sQuery(id+"F0.wireOp",EDGE,"E1.top");var subQ8=sQuery(id+"F0.wireOp",EDGE,"E1.left");var subQ9=sQuery(id+"F0.wireOp",EDGE,"E1.right");var subQ10=sQuery(id+"F0.wireOp",EDGE,"E23.filletArc");var subQ11=sQuery(id+"F0.wireOp",EDGE,"E24.filletArc");Q0=makeQuery(id+"F2.boolean.opBoolean","SPLIT",FACE,{"disambiguationData":[TD([makeQuery(id+"F1.opExtrude","SWEPT_FACE",FACE,{"disambiguationData":[OSD([subQ5])]})])],"derivedFrom":makeQuery(id+"F1.opExtrude","CAP_FACE",FACE,{"disambiguationData":[OSD([subQ5,subQ7,subQ8,subQ9,subQ4,subQ3,subQ2,subQ1,subQ6,subQ0,subQ10,subQ11])],"isStart":true})});}
            var sketch = newSketch(context, id + "F16", { "sketchPlane" : qUnion([Q0])});
            skLineSegment(sketch, "E79", {"start": v(-30.26, 74.25) * mm, "end": v(-12.26, 92.25) * mm});
            skLineSegment(sketch, "E80", {"start": v(-12.26, 92.25) * mm, "end": v(-12.26, 104.25) * mm});
            skLineSegment(sketch, "E81", {"start": v(35.74, 74.25) * mm, "end": v(17.74, 92.25) * mm});
            skLineSegment(sketch, "E82", {"start": v(17.74, 92.25) * mm, "end": v(17.74, 104.25) * mm});
            skArc(sketch, "E83", {"start": v(17.74, 104.25) * mm, "mid": v(2.74, 119.25) * mm, "end": v(-12.26, 104.25) * mm});
            skCircle(sketch, "E84", {"center": v(2.74, 104.25) * mm, "radius": 6 * mm});
            skLineSegment(sketch, "E85", {"start": v(2.74, 104.25) * mm, "end": v(2.74, 74.25) * mm, "construction": true});
            skLineSegment(sketch, "E86", {"start": v(-74.25, 0) * mm, "end": v(74.25, 0) * mm});
            skLineSegment(sketch, "E87.MirrorCS", {"start": v(-30.26, -74.25) * mm, "end": v(-12.26, -92.25) * mm});
            skLineSegment(sketch, "E88.MirrorCS", {"start": v(-12.26, -92.25) * mm, "end": v(-12.26, -104.25) * mm});
            skArc(sketch, "E89.MirrorCS", {"start": v(17.74, -104.25) * mm, "mid": v(2.74, -119.25) * mm, "end": v(-12.26, -104.25) * mm});
            skLineSegment(sketch, "E90.MirrorCS", {"start": v(17.74, -92.25) * mm, "end": v(17.74, -104.25) * mm});
            skCircle(sketch, "E91.MirrorC", {"center": v(2.74, -104.25) * mm, "radius": 6 * mm});
            skLineSegment(sketch, "E92.MirrorCS", {"start": v(35.74, -74.25) * mm, "end": v(17.74, -92.25) * mm});
            skSolve(sketch);
        }
        {
            var Q0;
            Q0=makeQuery(id+"F16.imprint","IMPRINT",FACE,{"disambiguationData":[TD([[makeQuery(id+"F16.imprint","IMPRINT",EDGE,{"derivedFrom":makeQuery(id+"F1.opExtrude","CAP_EDGE",EDGE,{"disambiguationData":[OSD([sQuery(id+"F0.wireOp",EDGE,"E4")])],"isStart":true})}),-1.0]])]});
            var Q1;
            {var subQ1=sQuery(id+"F16.wireOp",EDGE,"E79");Q1=makeQuery(id+"F16.imprint","IMPRINT",FACE,{"disambiguationData":[TD([[makeQuery(id+"F16.imprint","IMPRINT",EDGE,{"derivedFrom":subQ1}),-1.0]])]});}
            var Q2;
            Q2=makeQuery(id+"F16.imprint","IMPRINT",FACE,{"disambiguationData":[TD([[makeQuery(id+"F16.imprint","IMPRINT",EDGE,{"derivedFrom":makeQuery(id+"F1.opExtrude","CAP_EDGE",EDGE,{"disambiguationData":[OSD([sQuery(id+"F0.wireOp",EDGE,"E6")])],"isStart":true})}),-1.0]])]});
            var Q3;
            {var subQ0=sQuery(id+"F16.wireOp",EDGE,"E87.MirrorCS");Q3=makeQuery(id+"F16.imprint","IMPRINT",FACE,{"disambiguationData":[TD([[makeQuery(id+"F16.imprint","IMPRINT",EDGE,{"derivedFrom":subQ0}),1.0]])]});}
            var Q4;
            Q4=makeQuery(id+"F2.opExtrude","CAP_FACE",FACE,{"disambiguationData":[OSD([sQuery(id+"F0.wireOp",EDGE,"E12"),sQuery(id+"F0.wireOp",EDGE,"E13"),sQuery(id+"F0.wireOp",EDGE,"E14"),sQuery(id+"F0.wireOp",EDGE,"E15"),sQuery(id+"F0.wireOp",EDGE,"E17.filletArc"),sQuery(id+"F0.wireOp",EDGE,"E18.filletArc"),sQuery(id+"F0.wireOp",EDGE,"E19.filletArc"),sQuery(id+"F0.wireOp",EDGE,"E20.filletArc"),sQuery(id+"F0.wireOp",EDGE,"E25.0"),sQuery(id+"F0.wireOp",EDGE,"E25.1"),sQuery(id+"F0.wireOp",EDGE,"E25.2"),sQuery(id+"F0.wireOp",EDGE,"E25.3"),sQuery(id+"F0.wireOp",EDGE,"E25.4"),sQuery(id+"F0.wireOp",EDGE,"E25.5"),sQuery(id+"F0.wireOp",EDGE,"E25.6"),sQuery(id+"F0.wireOp",EDGE,"E25.7")])],"isStart":false});
            extrude(context, id + "F17", {"entities" : qUnion([Q0, Q1, Q2, Q3]), "operationType" : NewBodyOperationType.ADD, "endBound" : BoundingType.UP_TO_SURFACE, "endBoundEntityFace" : qUnion([Q4]), "depth" : 25 * mm});
        }
    });
